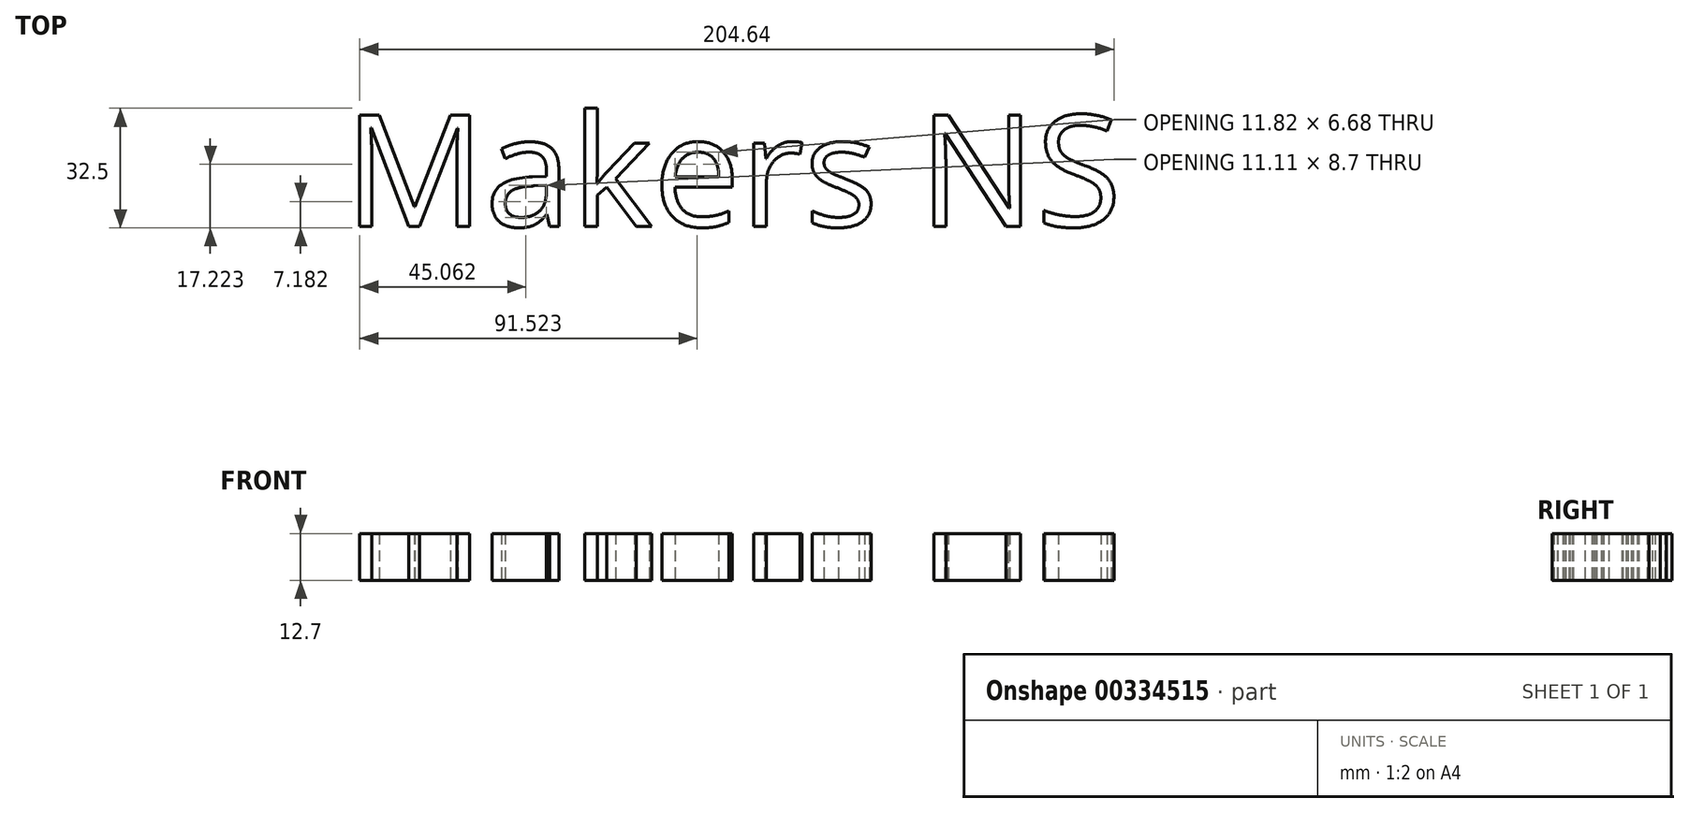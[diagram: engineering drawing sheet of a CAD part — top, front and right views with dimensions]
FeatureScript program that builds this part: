
annotation { "Feature Type Name" : "Feature", "Feature Type Description" : "" }
export const myFeature = defineFeature(function(context is Context, id is Id, definition is map)
    precondition{}
    {
        {
            var Q0;
            Q0=qCreatedBy(makeId("Top.planeOp"),FACE);
            var sketch = newSketch(context, id + "F0", { "sketchPlane" : qUnion([Q0])});
            skText(sketch, "E0", { "text": "Makers NS", "fontName": "OpenSans-Regular.ttf"});
            const initialGuessF0  = {"E0": [-0.04448, -0.0304, 1, 0, 0.0304]};
            skSetInitialGuess(sketch, initialGuessF0);
            skSolve(sketch);
        }
        {
            var Q0;
            Q0 = qSketchRegion(id + "F0", true);
            extrude(context, id + "F1", {"entities" : qUnion([Q0]), "depth" : 12.7 * mm});
        }
    });
